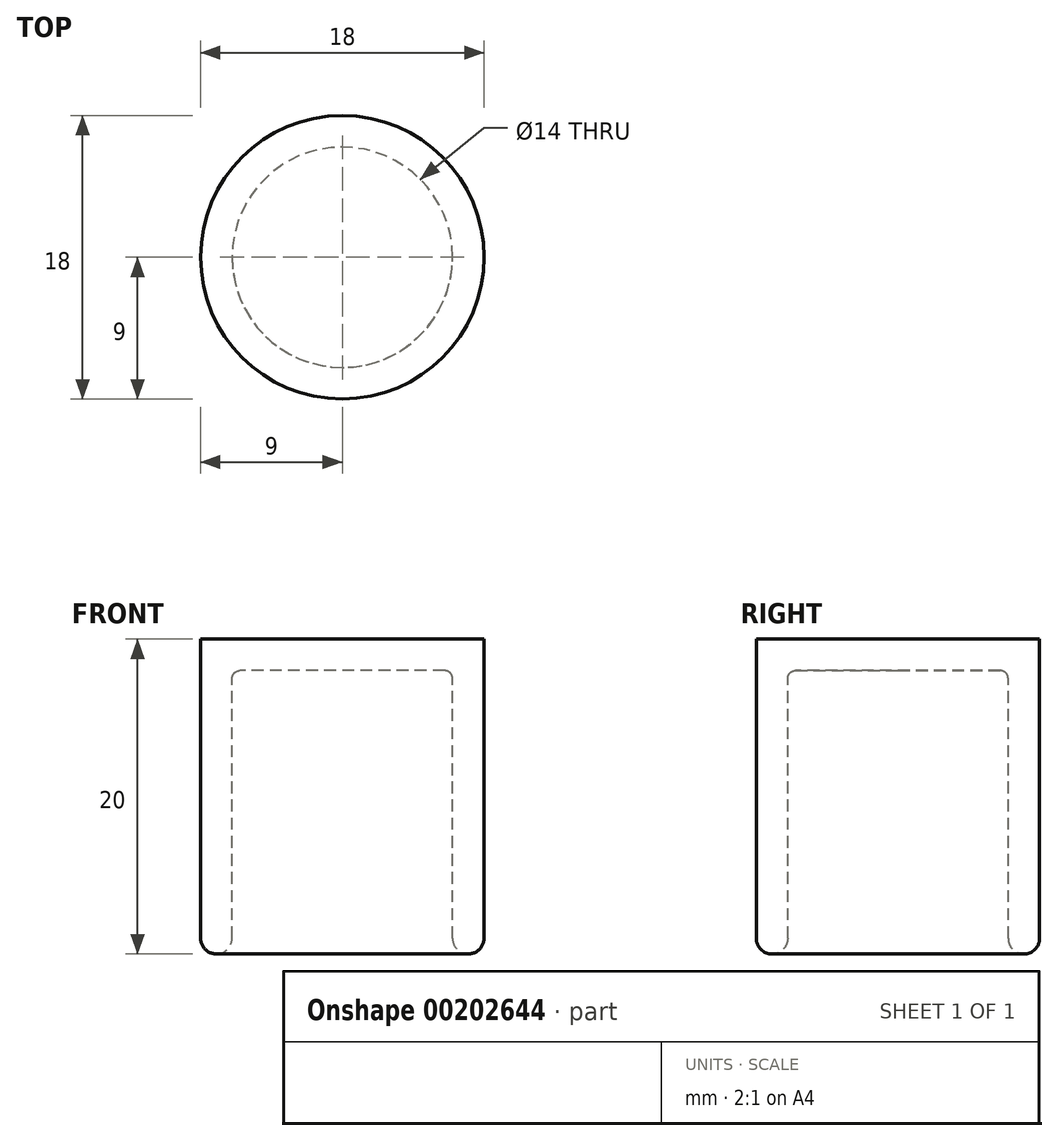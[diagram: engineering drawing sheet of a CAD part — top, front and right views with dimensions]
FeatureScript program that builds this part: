
annotation { "Feature Type Name" : "Feature", "Feature Type Description" : "" }
export const myFeature = defineFeature(function(context is Context, id is Id, definition is map)
    precondition{}
    {
        {
            var Q0;
            Q0=qCreatedBy(makeId("Front.planeOp"),FACE);
            var sketch = newSketch(context, id + "F0", { "sketchPlane" : qUnion([Q0])});
            skLineSegment(sketch, "E0", {"start": v(0, 14.7) * mm, "end": v(0, -5.3) * mm, "construction": true});
            skLineSegment(sketch, "E1", {"start": v(0, 14.7) * mm, "end": v(-9, 14.7) * mm});
            skLineSegment(sketch, "E2", {"start": v(-9, 14.7) * mm, "end": v(-9, -5.3) * mm});
            skLineSegment(sketch, "E3", {"start": v(-9, -5.3) * mm, "end": v(-7, -5.3) * mm});
            skLineSegment(sketch, "E4.0", {"start": v(-7, 12.7) * mm, "end": v(-7, -5.3) * mm});
            skLineSegment(sketch, "E4.1", {"start": v(0, 12.7) * mm, "end": v(-7, 12.7) * mm});
            skLineSegment(sketch, "E5", {"start": v(0, 14.7) * mm, "end": v(0, 12.7) * mm});
            skSolve(sketch);
        }
        {
            var Q0;
            Q0 = qSketchRegion(id + "F0", true);
            var Q1;
            Q1=sQuery(id+"F0.wireOp",EDGE,"E0");
            revolve(context, id + "F1", {"entities" : qUnion([Q0]), "axis" : qUnion([Q1]), "revolveType" : RevolveType.FULL});
        }
        {
            var Q0;
            Q0=makeQuery(id+"F1.opRevolve","SWEPT_EDGE",EDGE,{"disambiguationData":[OSD([sQuery(id+"F0.wireOp",EDGE,"E4.0"),sQuery(id+"F0.wireOp",EDGE,"E4.1")])]});
            fillet(context, id + "F2", {"entities" : qUnion([Q0]), "radius" : 0.5 * mm, "tangentPropagation" : true, "allowEdgeOverflow" : false});
        }
        {
            var Q0;
            Q0=makeQuery(id+"F1.opRevolve","SWEPT_FACE",FACE,{"disambiguationData":[OSD([sQuery(id+"F0.wireOp",EDGE,"E3")])]});
            fillet(context, id + "F3", {"entities" : qUnion([Q0]), "radius" : 1 * mm, "tangentPropagation" : true, "allowEdgeOverflow" : false});
        }
    });
